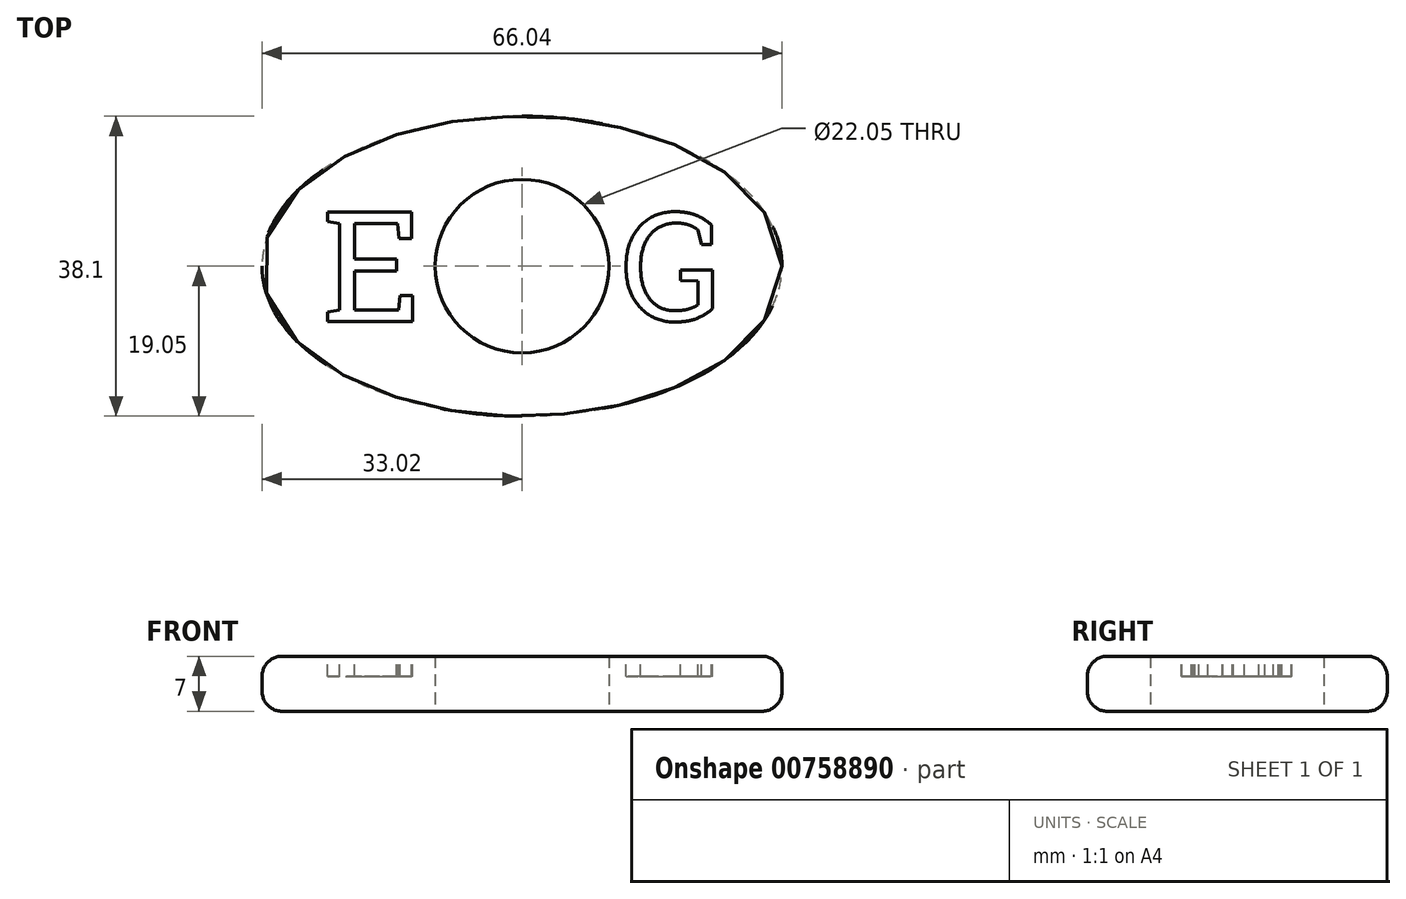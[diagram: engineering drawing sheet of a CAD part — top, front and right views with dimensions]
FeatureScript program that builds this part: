
annotation { "Feature Type Name" : "Feature", "Feature Type Description" : "" }
export const myFeature = defineFeature(function(context is Context, id is Id, definition is map)
    precondition{}
    {
        {
            var Q0;
            Q0=qCreatedBy(makeId("Top.planeOp"),FACE);
            var sketch = newSketch(context, id + "F0", { "sketchPlane" : qUnion([Q0])});
            skEllipse(sketch, "E0", {"center": v(0, 0) * mm, "majorRadius": 33.02 * mm, "minorRadius": 19.05 * mm, "majorAxis": v(1, 0)});
            skCircle(sketch, "E1", {"center": v(0, 0) * mm, "radius": 11.03 * mm});
            skLineSegment(sketch, "E2", {"start": v(-33.02, 0) * mm, "end": v(33.02, 0) * mm, "construction": true});
            skLineSegment(sketch, "E3", {"start": v(0, 19.05) * mm, "end": v(0, -19.05) * mm, "construction": true});
            skSolve(sketch);
        }
        {
            var Q0;
            Q0=makeQuery(id+"F0.imprint","IMPRINT",FACE,{"disambiguationData":[TD([[makeQuery(id+"F0.imprint","IMPRINT",EDGE,{"derivedFrom":sQuery(id+"F0.wireOp",EDGE,"E0")}),1.0]])]});
            extrude(context, id + "F1", {"entities" : qUnion([Q0]), "depth" : 7 * mm, "offsetDistance" : 25.4 * mm});
        }
        {
            var Q0;
            Q0=makeQuery(id+"F1.opExtrude","CAP_EDGE",EDGE,{"disambiguationData":[OSD([sQuery(id+"F0.wireOp",EDGE,"E0")])],"isStart":false});
            var Q1;
            Q1=makeQuery(id+"F1.opExtrude","CAP_EDGE",EDGE,{"disambiguationData":[OSD([sQuery(id+"F0.wireOp",EDGE,"E0")])],"isStart":true});
            fillet(context, id + "F2", {"entities" : qUnion([Q0, Q1]), "radius" : 2.54 * mm, "tangentPropagation" : true, "allowEdgeOverflow" : false});
        }
        {
            var Q0;
            Q0=makeQuery(id+"F1.opExtrude","CAP_FACE",FACE,{"disambiguationData":[OSD([sQuery(id+"F0.wireOp",EDGE,"E0"),sQuery(id+"F0.wireOp",EDGE,"E1")])],"isStart":false});
            var sketch = newSketch(context, id + "F3", { "sketchPlane" : qUnion([Q0])});
            skSolve(sketch);
        }
        {
            var Q0;
            {var subQ0=sQuery(id+"F0.wireOp",EDGE,"E1");Q0=makeQuery(id+"F3.imprint","IMPRINT",FACE,{"disambiguationData":[TD([[makeQuery(id+"F3.imprint","IMPRINT",EDGE,{"derivedFrom":makeQuery(id+"F1.opExtrude","CAP_EDGE",EDGE,{"disambiguationData":[OSD([subQ0])],"isStart":false})}),-1.0]])]});}
            var sketch = newSketch(context, id + "F4", { "sketchPlane" : qUnion([Q0])});
            skText(sketch, "E4", { "text": "E", "fontName": "RobotoSlab-Regular.ttf"});
            skText(sketch, "E5", { "text": "G", "fontName": "RobotoSlab-Regular.ttf"});
            skLineSegment(sketch, "E6", {"start": v(0, 0) * mm, "end": v(-25.4, 0) * mm, "construction": true});
            skLineSegment(sketch, "E7", {"start": v(0, 0) * mm, "end": v(25.4, 0) * mm, "construction": true});
            skLineSegment(sketch, "E8", {"start": v(-25.4, 0) * mm, "end": v(-12.7, 0) * mm, "construction": true});
            skLineSegment(sketch, "E9", {"start": v(12.7, 0) * mm, "end": v(25.4, 0) * mm});
            skPoint(sketch, "E10", {"position": v(19.05, 0) * mm});
            skLineSegment(sketch, "E11", {"start": v(12.7, 0) * mm, "end": v(25.4, 0) * mm, "construction": true});
            skPoint(sketch, "E12", {"position": v(-19.05, 0) * mm});
            const initialGuessF4  = {"E4": [-0.0254, -0.00706, 1, 0, 0.01411], "E5": [0.0127, -0.0069, 1, 0, 0.0138]};
            skSetInitialGuess(sketch, initialGuessF4);
            skSolve(sketch);
        }
        {
            var Q0;
            Q0=qSketchRegion(id+"F4",true);
            extrude(context, id + "F5", {"entities" : qUnion([Q0]), "operationType" : NewBodyOperationType.REMOVE, "oppositeDirection" : true, "depth" : 2.54 * mm, "offsetDistance" : 25.4 * mm});
        }
    });
